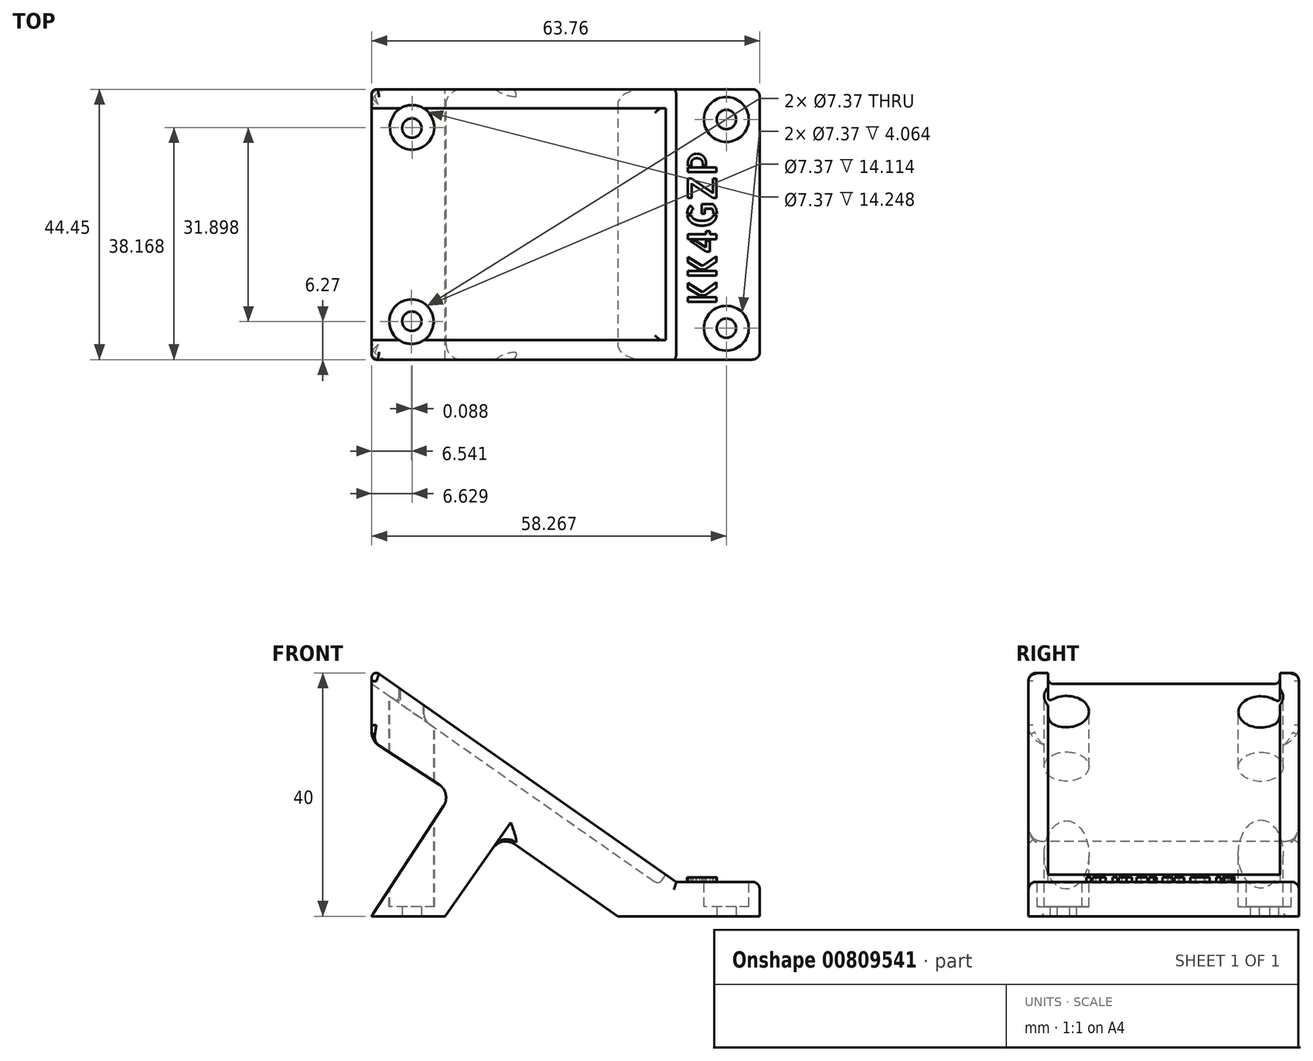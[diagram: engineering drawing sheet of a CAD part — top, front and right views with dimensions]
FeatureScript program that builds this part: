
annotation { "Feature Type Name" : "Feature", "Feature Type Description" : "" }
export const myFeature = defineFeature(function(context is Context, id is Id, definition is map)
    precondition{}
    {
        {
            var Q0;
            Q0=qCreatedBy(makeId("Top.planeOp"),FACE);
            var sketch = newSketch(context, id + "F0", { "sketchPlane" : qUnion([Q0])});
            skPoint(sketch, "E0.middle", {"position": v(0, 0) * mm});
            skCircle(sketch, "E1", {"center": v(-26.75, 16.45) * mm, "radius": 1.59 * mm});
            skCircle(sketch, "E2", {"center": v(-26.75, -15.3) * mm, "radius": 1.59 * mm});
            skCircle(sketch, "E3", {"center": v(24.92, 17.87) * mm, "radius": 1.59 * mm});
            skCircle(sketch, "E4", {"center": v(24.92, -16.44) * mm, "radius": 1.59 * mm});
            skLineSegment(sketch, "E5.0", {"start": v(30.4, 22.84) * mm, "end": v(-33.35, 22.84) * mm});
            skLineSegment(sketch, "E5.1", {"start": v(30.4, 22.84) * mm, "end": v(30.4, -21.6) * mm});
            skLineSegment(sketch, "E5.2", {"start": v(30.4, -21.6) * mm, "end": v(-33.35, -21.6) * mm});
            skLineSegment(sketch, "E5.3", {"start": v(-33.35, 22.84) * mm, "end": v(-33.35, -21.6) * mm});
            skSolve(sketch);
        }
        {
            var Q0;
            Q0=makeQuery(id+"F0.imprint","IMPRINT",FACE,{"disambiguationData":[TD([[makeQuery(id+"F0.imprint","IMPRINT",EDGE,{"derivedFrom":sQuery(id+"F0.wireOp",EDGE,"E1")}),-1.0]])]});
            extrude(context, id + "F1", {"entities" : qUnion([Q0]), "depth" : 50.8 * mm, "offsetDistance" : 25.4 * mm});
        }
        {
            var Q0;
            Q0=qCreatedBy(makeId("Front.planeOp"),FACE);
            var sketch = newSketch(context, id + "F2", { "sketchPlane" : qUnion([Q0])});
            skLineSegment(sketch, "E6", {"start": v(-55.66, 56.32) * mm, "end": v(16.7, 5.65) * mm});
            skLineSegment(sketch, "E7", {"start": v(16.7, 5.65) * mm, "end": v(44.17, 5.65) * mm});
            skLineSegment(sketch, "E8", {"start": v(44.17, 5.65) * mm, "end": v(44.17, 60.47) * mm});
            skLineSegment(sketch, "E9", {"start": v(44.17, 60.47) * mm, "end": v(-55.66, 56.32) * mm});
            skSolve(sketch);
        }
        {
            var Q0;
            Q0=makeQuery(id+"F2.imprint","IMPRINT",FACE,{"disambiguationData":[TD([[makeQuery(id+"F2.imprint","IMPRINT",EDGE,{"derivedFrom":sQuery(id+"F2.wireOp",EDGE,"E6")}),1.0]])]});
            extrude(context, id + "F3", {"entities" : qUnion([Q0]), "operationType" : NewBodyOperationType.REMOVE, "oppositeDirection" : true, "depth" : 76.2 * mm, "offsetDistance" : 25.4 * mm, "symmetric" : true});
        }
        {
            var Q0;
            Q0=makeQuery(id+"F3.boolean.opBoolean","COPY",FACE,{"derivedFrom":makeQuery(id+"F3.opExtrude","SWEPT_FACE",FACE,{"disambiguationData":[OSD([sQuery(id+"F2.wireOp",EDGE,"E6")])]})});
            var sketch = newSketch(context, id + "F4", { "sketchPlane" : qUnion([Q0])});
            skLineSegment(sketch, "E10.bottom", {"start": v(-54.48, 19.71) * mm, "end": v(8.35, 19.71) * mm});
            skLineSegment(sketch, "E10.top", {"start": v(-54.48, -18.39) * mm, "end": v(8.35, -18.39) * mm});
            skLineSegment(sketch, "E10.left", {"start": v(-54.48, 19.71) * mm, "end": v(-54.48, -18.39) * mm});
            skLineSegment(sketch, "E10.right", {"start": v(8.35, 19.71) * mm, "end": v(8.35, -18.39) * mm});
            skSolve(sketch);
        }
        {
            var Q0;
            Q0 = qSketchRegion(id + "F4", true);
            extrude(context, id + "F5", {"entities" : qUnion([Q0]), "operationType" : NewBodyOperationType.REMOVE, "oppositeDirection" : true, "depth" : 2.03 * mm, "offsetDistance" : 25.4 * mm});
        }
        {
            var Q0;
            Q0=makeQuery(id+"F3.boolean.opBoolean","COPY",FACE,{"derivedFrom":makeQuery(id+"F3.opExtrude","SWEPT_FACE",FACE,{"disambiguationData":[OSD([sQuery(id+"F2.wireOp",EDGE,"E7")])]})});
            var sketch = newSketch(context, id + "F6", { "sketchPlane" : qUnion([Q0])});
            skCircle(sketch, "E11", {"center": v(24.92, 17.87) * mm, "radius": 3.68 * mm});
            skCircle(sketch, "E12", {"center": v(24.92, -16.44) * mm, "radius": 3.68 * mm});
            skCircle(sketch, "E13", {"center": v(-26.8, -15.34) * mm, "radius": 3.68 * mm});
            skCircle(sketch, "E14", {"center": v(-26.72, 16.56) * mm, "radius": 3.68 * mm});
            skSolve(sketch);
        }
        {
            var Q0;
            Q0 = qSketchRegion(id + "F6", true);
            extrude(context, id + "F7", {"entities" : qUnion([Q0]), "operationType" : NewBodyOperationType.REMOVE, "oppositeDirection" : true, "depth" : 4.06 * mm, "offsetDistance" : 25.4 * mm, "hasSecondDirection" : true, "secondDirectionOppositeDirection" : false, "secondDirectionDepth" : 50.8 * mm});
        }
        {
            var Q0;
            Q0=makeQuery(id+"F3.boolean.opBoolean","INTERSECT",EDGE,{"derivedFrom":[makeQuery(id+"F1.opExtrude","SWEPT_FACE",FACE,{"disambiguationData":[OSD([sQuery(id+"F0.wireOp",EDGE,"E5.2")])]}),makeQuery(id+"F3.opExtrude","SWEPT_FACE",FACE,{"disambiguationData":[OSD([sQuery(id+"F2.wireOp",EDGE,"E7")])]})]});
            var Q1;
            Q1=makeQuery(id+"FOz7J2DfmrePzTN_1.boolean.opBoolean","INTERSECT",EDGE,{"derivedFrom":[makeQuery(id+"F1.opExtrude","SWEPT_FACE",FACE,{"disambiguationData":[OSD([sQuery(id+"F0.wireOp",EDGE,"E5.2")])]}),makeQuery(id+"FOz7J2DfmrePzTN_1.opExtrude","SWEPT_FACE",FACE,{"disambiguationData":[OSD([sQuery(id+"FwJpcnfpDOWBhRW_1.wireOp",EDGE,"7TAsQrwD-nJ7S-N01j-4NwB-wfjMZ5C82BP1")])]})]});
            var Q2;
            Q2=makeQuery(id+"FOz7J2DfmrePzTN_1.boolean.opBoolean","INTERSECT",EDGE,{"derivedFrom":[makeQuery(id+"F1.opExtrude","SWEPT_FACE",FACE,{"disambiguationData":[OSD([sQuery(id+"F0.wireOp",EDGE,"E5.2")])]}),makeQuery(id+"FOz7J2DfmrePzTN_1.opExtrude","SWEPT_FACE",FACE,{"disambiguationData":[OSD([sQuery(id+"FwJpcnfpDOWBhRW_1.wireOp",EDGE,"6dGtPzXd-V9vu-5sIf-QmpP-IY3SuzzBftYZ")])]})]});
            var Q3;
            Q3=makeQuery(id+"FOz7J2DfmrePzTN_1.boolean.opBoolean","INTERSECT",EDGE,{"derivedFrom":[makeQuery(id+"F1.opExtrude","SWEPT_FACE",FACE,{"disambiguationData":[OSD([sQuery(id+"F0.wireOp",EDGE,"E5.2")])]}),makeQuery(id+"FOz7J2DfmrePzTN_1.opExtrude","SWEPT_FACE",FACE,{"disambiguationData":[OSD([sQuery(id+"FwJpcnfpDOWBhRW_1.wireOp",EDGE,"HFOe4aiu-vJgC-u0Dz-aEjB-NTL0ylJjOqHZ")])]})]});
            var Q4;
            Q4=makeQuery(id+"FOz7J2DfmrePzTN_1.boolean.opBoolean","INTERSECT",EDGE,{"derivedFrom":[makeQuery(id+"F1.opExtrude","SWEPT_FACE",FACE,{"disambiguationData":[OSD([sQuery(id+"F0.wireOp",EDGE,"E5.2")])]}),makeQuery(id+"FOz7J2DfmrePzTN_1.opExtrude","SWEPT_FACE",FACE,{"disambiguationData":[OSD([sQuery(id+"FwJpcnfpDOWBhRW_1.wireOp",EDGE,"6FotfcRq-kzrp-HAaR-29gi-kztGfECXmqdc")])]})]});
            var Q5;
            Q5=makeQuery(id+"Fn8nH9Q8Esl1Hek_1.boolean.opBoolean","INTERSECT",EDGE,{"derivedFrom":[makeQuery(id+"F1.opExtrude","SWEPT_FACE",FACE,{"disambiguationData":[OSD([sQuery(id+"F0.wireOp",EDGE,"E5.2")])]}),makeQuery(id+"Fn8nH9Q8Esl1Hek_1.opExtrude","SWEPT_FACE",FACE,{"disambiguationData":[OSD([sQuery(id+"F2zjoIBAfDjMboZ_1.wireOp",EDGE,"NsKbtacR-0WmU-dClk-nRrQ-DuOnGeB0pbxx")])]})]});
            var Q6;
            Q6=makeQuery(id+"Fn8nH9Q8Esl1Hek_1.boolean.opBoolean","INTERSECT",EDGE,{"derivedFrom":[makeQuery(id+"F1.opExtrude","SWEPT_FACE",FACE,{"disambiguationData":[OSD([sQuery(id+"F0.wireOp",EDGE,"E5.0")])]}),makeQuery(id+"Fn8nH9Q8Esl1Hek_1.opExtrude","SWEPT_FACE",FACE,{"disambiguationData":[OSD([sQuery(id+"F2zjoIBAfDjMboZ_1.wireOp",EDGE,"NsKbtacR-0WmU-dClk-nRrQ-DuOnGeB0pbxx")])]})]});
            var Q7;
            Q7=makeQuery(id+"F3.boolean.opBoolean","INTERSECT",EDGE,{"derivedFrom":[makeQuery(id+"F1.opExtrude","SWEPT_FACE",FACE,{"disambiguationData":[OSD([sQuery(id+"F0.wireOp",EDGE,"E5.0")])]}),makeQuery(id+"F3.opExtrude","SWEPT_FACE",FACE,{"disambiguationData":[OSD([sQuery(id+"F2.wireOp",EDGE,"E6")])]})]});
            var Q8;
            Q8=makeQuery(id+"F3.boolean.opBoolean","INTERSECT",EDGE,{"derivedFrom":[makeQuery(id+"F1.opExtrude","SWEPT_FACE",FACE,{"disambiguationData":[OSD([sQuery(id+"F0.wireOp",EDGE,"E5.0")])]}),makeQuery(id+"F3.opExtrude","SWEPT_FACE",FACE,{"disambiguationData":[OSD([sQuery(id+"F2.wireOp",EDGE,"E7")])]})]});
            var Q9;
            Q9=makeQuery(id+"FOz7J2DfmrePzTN_1.boolean.opBoolean","INTERSECT",EDGE,{"derivedFrom":[makeQuery(id+"F1.opExtrude","SWEPT_FACE",FACE,{"disambiguationData":[OSD([sQuery(id+"F0.wireOp",EDGE,"E5.0")])]}),makeQuery(id+"FOz7J2DfmrePzTN_1.opExtrude","SWEPT_FACE",FACE,{"disambiguationData":[OSD([sQuery(id+"FwJpcnfpDOWBhRW_1.wireOp",EDGE,"HFOe4aiu-vJgC-u0Dz-aEjB-NTL0ylJjOqHZ")])]})]});
            var Q10;
            Q10=makeQuery(id+"FOz7J2DfmrePzTN_1.boolean.opBoolean","INTERSECT",EDGE,{"derivedFrom":[makeQuery(id+"F1.opExtrude","SWEPT_FACE",FACE,{"disambiguationData":[OSD([sQuery(id+"F0.wireOp",EDGE,"E5.0")])]}),makeQuery(id+"FOz7J2DfmrePzTN_1.opExtrude","SWEPT_FACE",FACE,{"disambiguationData":[OSD([sQuery(id+"FwJpcnfpDOWBhRW_1.wireOp",EDGE,"6dGtPzXd-V9vu-5sIf-QmpP-IY3SuzzBftYZ")])]})]});
            var Q11;
            Q11=makeQuery(id+"FOz7J2DfmrePzTN_1.boolean.opBoolean","INTERSECT",EDGE,{"derivedFrom":[makeQuery(id+"F1.opExtrude","SWEPT_FACE",FACE,{"disambiguationData":[OSD([sQuery(id+"F0.wireOp",EDGE,"E5.0")])]}),makeQuery(id+"FOz7J2DfmrePzTN_1.opExtrude","SWEPT_FACE",FACE,{"disambiguationData":[OSD([sQuery(id+"FwJpcnfpDOWBhRW_1.wireOp",EDGE,"7TAsQrwD-nJ7S-N01j-4NwB-wfjMZ5C82BP1")])]})]});
            var Q12;
            Q12=makeQuery(id+"FOz7J2DfmrePzTN_1.boolean.opBoolean","INTERSECT",EDGE,{"derivedFrom":[makeQuery(id+"F1.opExtrude","SWEPT_FACE",FACE,{"disambiguationData":[OSD([sQuery(id+"F0.wireOp",EDGE,"E5.0")])]}),makeQuery(id+"FOz7J2DfmrePzTN_1.opExtrude","SWEPT_FACE",FACE,{"disambiguationData":[OSD([sQuery(id+"FwJpcnfpDOWBhRW_1.wireOp",EDGE,"6FotfcRq-kzrp-HAaR-29gi-kztGfECXmqdc")])]})]});
            var Q13;
            Q13=makeQuery(id+"F1.opExtrude","CAP_EDGE",EDGE,{"disambiguationData":[OSD([sQuery(id+"F0.wireOp",EDGE,"E5.0")])],"isStart":false});
            var Q14;
            Q14=makeQuery(id+"F1.opExtrude","CAP_EDGE",EDGE,{"disambiguationData":[OSD([sQuery(id+"F0.wireOp",EDGE,"E5.2")])],"isStart":false});
            var Q15;
            Q15=makeQuery(id+"F3.boolean.opBoolean","INTERSECT",EDGE,{"derivedFrom":[makeQuery(id+"F1.opExtrude","SWEPT_FACE",FACE,{"disambiguationData":[OSD([sQuery(id+"F0.wireOp",EDGE,"E5.2")])]}),makeQuery(id+"F3.opExtrude","SWEPT_FACE",FACE,{"disambiguationData":[OSD([sQuery(id+"F2.wireOp",EDGE,"E6")])]})]});
            fillet(context, id + "F8", {"entities" : qUnion([Q0, Q1, Q2, Q3, Q4, Q5, Q6, Q7, Q8, Q9, Q10, Q11, Q12, Q13, Q14, Q15]), "radius" : 1.27 * mm, "tangentPropagation" : true, "allowEdgeOverflow" : false});
        }
        {
            var Q0;
            Q0=qCreatedBy(makeId("Front.planeOp"),FACE);
            var sketch = newSketch(context, id + "F9", { "sketchPlane" : qUnion([Q0])});
            skLineSegment(sketch, "E15.0", {"start": v(11.2, -2.9) * mm, "end": v(-11.94, 13.31) * mm});
            skLineSegment(sketch, "E16", {"start": v(-20.87, -3.55) * mm, "end": v(11.2, -2.9) * mm});
            skLineSegment(sketch, "E17", {"start": v(-11.94, 13.31) * mm, "end": v(-23.91, -3.78) * mm});
            skLineSegment(sketch, "E18", {"start": v(-20.87, -3.55) * mm, "end": v(-23.91, -3.78) * mm});
            skSolve(sketch);
        }
        {
            var Q0;
            Q0 = qSketchRegion(id + "F9", true);
            extrude(context, id + "F10", {"entities" : qUnion([Q0]), "operationType" : NewBodyOperationType.REMOVE, "depth" : 76.2 * mm, "offsetDistance" : 25.4 * mm, "symmetric" : true});
        }
        {
            var Q0;
            Q0=makeQuery(id+"F10.boolean.opBoolean","INTERSECT",EDGE,{"derivedFrom":[makeQuery(id+"F1.opExtrude","SWEPT_FACE",FACE,{"disambiguationData":[OSD([sQuery(id+"F0.wireOp",EDGE,"E5.2")])]}),makeQuery(id+"F10.opExtrude","SWEPT_FACE",FACE,{"disambiguationData":[OSD([sQuery(id+"F9.wireOp",EDGE,"E15.0")])]})]});
            var Q1;
            Q1=makeQuery(id+"F10.boolean.opBoolean","INTERSECT",EDGE,{"derivedFrom":[makeQuery(id+"F1.opExtrude","SWEPT_FACE",FACE,{"disambiguationData":[OSD([sQuery(id+"F0.wireOp",EDGE,"E5.2")])]}),makeQuery(id+"F10.opExtrude","SWEPT_FACE",FACE,{"disambiguationData":[OSD([sQuery(id+"F9.wireOp",EDGE,"ccf1a9ce-37c2-4cbf-8fa8-a78777553da6.0")])]})]});
            var Q2;
            Q2=makeQuery(id+"F10.boolean.opBoolean","INTERSECT",EDGE,{"derivedFrom":[makeQuery(id+"F1.opExtrude","SWEPT_FACE",FACE,{"disambiguationData":[OSD([sQuery(id+"F0.wireOp",EDGE,"E5.0")])]}),makeQuery(id+"F10.opExtrude","SWEPT_FACE",FACE,{"disambiguationData":[OSD([sQuery(id+"F9.wireOp",EDGE,"ccf1a9ce-37c2-4cbf-8fa8-a78777553da6.0")])]})]});
            var Q3;
            Q3=makeQuery(id+"F10.boolean.opBoolean","INTERSECT",EDGE,{"derivedFrom":[makeQuery(id+"F1.opExtrude","SWEPT_FACE",FACE,{"disambiguationData":[OSD([sQuery(id+"F0.wireOp",EDGE,"E5.0")])]}),makeQuery(id+"F10.opExtrude","SWEPT_FACE",FACE,{"disambiguationData":[OSD([sQuery(id+"F9.wireOp",EDGE,"E15.0")])]})]});
            fillet(context, id + "F11", {"entities" : qUnion([Q0, Q1, Q2, Q3]), "radius" : 2.54 * mm, "tangentPropagation" : true, "allowEdgeOverflow" : false});
        }
        {
            var Q0;
            Q0=makeQuery(id+"F5.boolean.opBoolean","COPY",EDGE,{"derivedFrom":makeQuery(id+"F5.opExtrude","CAP_EDGE",EDGE,{"disambiguationData":[OSD([sQuery(id+"F4.wireOp",EDGE,"E10.right")])],"isStart":true})});
            var Q1;
            Q1=makeQuery(id+"F5.boolean.opBoolean","COPY",EDGE,{"derivedFrom":makeQuery(id+"F5.opExtrude","CAP_EDGE",EDGE,{"disambiguationData":[OSD([sQuery(id+"F4.wireOp",EDGE,"E10.bottom")])],"isStart":true})});
            var Q2;
            Q2=makeQuery(id+"F5.boolean.opBoolean","COPY",EDGE,{"derivedFrom":makeQuery(id+"F5.opExtrude","CAP_EDGE",EDGE,{"disambiguationData":[OSD([sQuery(id+"F4.wireOp",EDGE,"E10.top")])],"isStart":true})});
            var Q3;
            Q3=makeQuery(id+"F5.boolean.opBoolean","COPY",EDGE,{"derivedFrom":makeQuery(id+"F5.opExtrude","CAP_EDGE",EDGE,{"disambiguationData":[OSD([sQuery(id+"F4.wireOp",EDGE,"E10.right")])],"isStart":false})});
            var Q4;
            Q4=makeQuery(id+"F5.boolean.opBoolean","COPY",EDGE,{"derivedFrom":makeQuery(id+"F5.opExtrude","CAP_EDGE",EDGE,{"disambiguationData":[OSD([sQuery(id+"F4.wireOp",EDGE,"E10.bottom")])],"isStart":false})});
            var Q5;
            Q5=makeQuery(id+"F5.boolean.opBoolean","COPY",EDGE,{"derivedFrom":makeQuery(id+"F5.opExtrude","CAP_EDGE",EDGE,{"disambiguationData":[OSD([sQuery(id+"F4.wireOp",EDGE,"E10.top")])],"isStart":false})});
            var Q6;
            Q6=makeQuery(id+"F5.boolean.opBoolean","INTERSECT",EDGE,{"derivedFrom":[makeQuery(id+"F1.opExtrude","CAP_FACE",FACE,{"disambiguationData":[OSD([sQuery(id+"F0.wireOp",EDGE,"E1"),sQuery(id+"F0.wireOp",EDGE,"E2"),sQuery(id+"F0.wireOp",EDGE,"E3"),sQuery(id+"F0.wireOp",EDGE,"E4"),sQuery(id+"F0.wireOp",EDGE,"E5.0"),sQuery(id+"F0.wireOp",EDGE,"E5.1"),sQuery(id+"F0.wireOp",EDGE,"E5.2"),sQuery(id+"F0.wireOp",EDGE,"E5.3")])],"isStart":false}),makeQuery(id+"F5.opExtrude","SWEPT_FACE",FACE,{"disambiguationData":[OSD([sQuery(id+"F4.wireOp",EDGE,"E10.top")])]})]});
            var Q7;
            Q7=makeQuery(id+"F5.boolean.opBoolean","INTERSECT",EDGE,{"derivedFrom":[makeQuery(id+"F1.opExtrude","CAP_FACE",FACE,{"disambiguationData":[OSD([sQuery(id+"F0.wireOp",EDGE,"E1"),sQuery(id+"F0.wireOp",EDGE,"E2"),sQuery(id+"F0.wireOp",EDGE,"E3"),sQuery(id+"F0.wireOp",EDGE,"E4"),sQuery(id+"F0.wireOp",EDGE,"E5.0"),sQuery(id+"F0.wireOp",EDGE,"E5.1"),sQuery(id+"F0.wireOp",EDGE,"E5.2"),sQuery(id+"F0.wireOp",EDGE,"E5.3")])],"isStart":false}),makeQuery(id+"F5.opExtrude","SWEPT_FACE",FACE,{"disambiguationData":[OSD([sQuery(id+"F4.wireOp",EDGE,"E10.bottom")])]})]});
            fillet(context, id + "F12", {"entities" : qUnion([Q0, Q1, Q2, Q3, Q4, Q5, Q6, Q7]), "radius" : 0.76 * mm, "tangentPropagation" : true, "allowEdgeOverflow" : false});
        }
        {
            var Q0;
            Q0=makeQuery(id+"F3.boolean.opBoolean","COPY",FACE,{"derivedFrom":makeQuery(id+"F3.opExtrude","SWEPT_FACE",FACE,{"disambiguationData":[OSD([sQuery(id+"F2.wireOp",EDGE,"E7")])]})});
            var sketch = newSketch(context, id + "F13", { "sketchPlane" : qUnion([Q0])});
            skText(sketch, "E19", { "text": "KK4GZP", "fontName": "AllertaStencil-Regular.ttf"});
            skPoint(sketch, "E20", {"position": v(27.25, 0) * mm});
            const initialGuessF13  = {"E19": [0.02331, -0.0127, 0, 1, 0.00475]};
            skSetInitialGuess(sketch, initialGuessF13);
            skSolve(sketch);
        }
        {
            var Q0;
            Q0 = qSketchRegion(id + "F13", true);
            extrude(context, id + "F14", {"entities" : qUnion([Q0]), "operationType" : NewBodyOperationType.ADD, "depth" : 0.76 * mm, "offsetDistance" : 25.4 * mm});
        }
        {
            var Q0;
            Q0=qCreatedBy(makeId("Front.planeOp"),FACE);
            var sketch = newSketch(context, id + "F15", { "sketchPlane" : qUnion([Q0])});
            skLineSegment(sketch, "E21", {"start": v(-41.67, 34.33) * mm, "end": v(-20.15, 20.25) * mm});
            skLineSegment(sketch, "E22", {"start": v(-20.15, 20.25) * mm, "end": v(-34.3, -1.36) * mm});
            skLineSegment(sketch, "E23", {"start": v(-34.3, -1.36) * mm, "end": v(-54.77, 18.88) * mm});
            skLineSegment(sketch, "E24", {"start": v(-54.77, 18.88) * mm, "end": v(-41.67, 34.33) * mm});
            skSolve(sketch);
        }
        {
            var Q0;
            Q0=makeQuery(id+"F15.imprint","IMPRINT",FACE,{"disambiguationData":[TD([[makeQuery(id+"F15.imprint","IMPRINT",EDGE,{"derivedFrom":sQuery(id+"F15.wireOp",EDGE,"E21")}),-1.0]])]});
            extrude(context, id + "F16", {"entities" : qUnion([Q0]), "operationType" : NewBodyOperationType.REMOVE, "oppositeDirection" : true, "depth" : 76.2 * mm, "offsetDistance" : 25.4 * mm, "symmetric" : true});
        }
        {
            var Q0;
            Q0=makeQuery(id+"F16.boolean.opBoolean","INTERSECT",EDGE,{"derivedFrom":[makeQuery(id+"F1.opExtrude","SWEPT_FACE",FACE,{"disambiguationData":[OSD([sQuery(id+"F0.wireOp",EDGE,"E5.2")])]}),makeQuery(id+"F16.opExtrude","SWEPT_FACE",FACE,{"disambiguationData":[OSD([sQuery(id+"F15.wireOp",EDGE,"E21")])]})]});
            var Q1;
            Q1=makeQuery(id+"F16.boolean.opBoolean","COPY",EDGE,{"derivedFrom":makeQuery(id+"F16.opExtrude","SWEPT_EDGE",EDGE,{"disambiguationData":[OSD([sQuery(id+"F15.wireOp",EDGE,"E21"),sQuery(id+"F15.wireOp",EDGE,"E22")])]})});
            var Q2;
            Q2=makeQuery(id+"F16.boolean.opBoolean","INTERSECT",EDGE,{"derivedFrom":[makeQuery(id+"F1.opExtrude","SWEPT_FACE",FACE,{"disambiguationData":[OSD([sQuery(id+"F0.wireOp",EDGE,"E5.2")])]}),makeQuery(id+"F16.opExtrude","SWEPT_FACE",FACE,{"disambiguationData":[OSD([sQuery(id+"F15.wireOp",EDGE,"E22")])]})]});
            var Q3;
            Q3=makeQuery(id+"F16.boolean.opBoolean","INTERSECT",EDGE,{"derivedFrom":[makeQuery(id+"F1.opExtrude","SWEPT_FACE",FACE,{"disambiguationData":[OSD([sQuery(id+"F0.wireOp",EDGE,"E5.0")])]}),makeQuery(id+"F16.opExtrude","SWEPT_FACE",FACE,{"disambiguationData":[OSD([sQuery(id+"F15.wireOp",EDGE,"E22")])]})]});
            var Q4;
            Q4=makeQuery(id+"F16.boolean.opBoolean","INTERSECT",EDGE,{"derivedFrom":[makeQuery(id+"F1.opExtrude","SWEPT_FACE",FACE,{"disambiguationData":[OSD([sQuery(id+"F0.wireOp",EDGE,"E5.0")])]}),makeQuery(id+"F16.opExtrude","SWEPT_FACE",FACE,{"disambiguationData":[OSD([sQuery(id+"F15.wireOp",EDGE,"E21")])]})]});
            var Q5;
            Q5=makeQuery(id+"F16.boolean.opBoolean","INTERSECT",EDGE,{"derivedFrom":[makeQuery(id+"F1.opExtrude","SWEPT_FACE",FACE,{"disambiguationData":[OSD([sQuery(id+"F0.wireOp",EDGE,"E5.3")])]}),makeQuery(id+"F16.opExtrude","SWEPT_FACE",FACE,{"disambiguationData":[OSD([sQuery(id+"F15.wireOp",EDGE,"E22")])]})]});
            var Q6;
            Q6=makeQuery(id+"F16.boolean.opBoolean","INTERSECT",EDGE,{"derivedFrom":[makeQuery(id+"F1.opExtrude","SWEPT_FACE",FACE,{"disambiguationData":[OSD([sQuery(id+"F0.wireOp",EDGE,"E5.3")])]}),makeQuery(id+"F16.opExtrude","SWEPT_FACE",FACE,{"disambiguationData":[OSD([sQuery(id+"F15.wireOp",EDGE,"E21")])]})]});
            var Q7;
            Q7=makeQuery(id+"F10.boolean.opBoolean","COPY",EDGE,{"derivedFrom":makeQuery(id+"F10.opExtrude","SWEPT_EDGE",EDGE,{"disambiguationData":[OSD([sQuery(id+"F9.wireOp",EDGE,"E15.0"),sQuery(id+"F9.wireOp",EDGE,"E17")])]})});
            fillet(context, id + "F17", {"entities" : qUnion([Q0, Q1, Q2, Q3, Q4, Q5, Q6, Q7]), "radius" : 2.54 * mm, "tangentPropagation" : true, "allowEdgeOverflow" : false});
        }
        {
            var Q0;
            Q0=makeQuery(id+"F3.boolean.opBoolean","INTERSECT",EDGE,{"derivedFrom":[makeQuery(id+"F1.opExtrude","SWEPT_FACE",FACE,{"disambiguationData":[OSD([sQuery(id+"F0.wireOp",EDGE,"E5.1")])]}),makeQuery(id+"F3.opExtrude","SWEPT_FACE",FACE,{"disambiguationData":[OSD([sQuery(id+"F2.wireOp",EDGE,"E7")])]})]});
            var Q1;
            Q1=makeQuery(id+"F8.opFillet","BLEND_EDGE",EDGE,{"blendedFrom":[makeQuery(id+"F3.boolean.opBoolean","INTERSECT",EDGE,{"derivedFrom":[makeQuery(id+"F1.opExtrude","SWEPT_FACE",FACE,{"disambiguationData":[OSD([sQuery(id+"F0.wireOp",EDGE,"E5.2")])]}),makeQuery(id+"F3.opExtrude","SWEPT_FACE",FACE,{"disambiguationData":[OSD([sQuery(id+"F2.wireOp",EDGE,"E7")])]})]}),makeQuery(id+"F1.opExtrude","SWEPT_FACE",FACE,{"disambiguationData":[OSD([sQuery(id+"F0.wireOp",EDGE,"E5.1")])]})],"blendedInto":[makeQuery(id+"F1.opExtrude","SWEPT_FACE",FACE,{"disambiguationData":[OSD([sQuery(id+"F0.wireOp",EDGE,"E5.1")])]})]});
            var Q2;
            Q2=makeQuery(id+"F1.opExtrude","SWEPT_EDGE",EDGE,{"disambiguationData":[OSD([sQuery(id+"F0.wireOp",EDGE,"E5.0"),sQuery(id+"F0.wireOp",EDGE,"E5.1")])]});
            var Q3;
            Q3=makeQuery(id+"F8.opFillet","BLEND_EDGE",EDGE,{"blendedFrom":[makeQuery(id+"F3.boolean.opBoolean","INTERSECT",EDGE,{"derivedFrom":[makeQuery(id+"F1.opExtrude","SWEPT_FACE",FACE,{"disambiguationData":[OSD([sQuery(id+"F0.wireOp",EDGE,"E5.0")])]}),makeQuery(id+"F3.opExtrude","SWEPT_FACE",FACE,{"disambiguationData":[OSD([sQuery(id+"F2.wireOp",EDGE,"E7")])]})]}),makeQuery(id+"F1.opExtrude","SWEPT_FACE",FACE,{"disambiguationData":[OSD([sQuery(id+"F0.wireOp",EDGE,"E5.1")])]})],"blendedInto":[makeQuery(id+"F1.opExtrude","SWEPT_FACE",FACE,{"disambiguationData":[OSD([sQuery(id+"F0.wireOp",EDGE,"E5.1")])]})]});
            var Q4;
            Q4=makeQuery(id+"F1.opExtrude","SWEPT_EDGE",EDGE,{"disambiguationData":[OSD([sQuery(id+"F0.wireOp",EDGE,"E5.1"),sQuery(id+"F0.wireOp",EDGE,"E5.2")])]});
            fillet(context, id + "F18", {"entities" : qUnion([Q0, Q1, Q2, Q3, Q4]), "radius" : 1.27 * mm, "tangentPropagation" : true, "allowEdgeOverflow" : false});
        }
        {
            var Q0;
            {var subQ0=sQuery(id+"F0.wireOp",EDGE,"E5.0");var subQ1=sQuery(id+"F0.wireOp",EDGE,"E5.3");Q0=makeQuery(id+"F16.boolean.opBoolean","SPLIT",EDGE,{"disambiguationData":[TD([makeQuery(id+"F16.opExtrude","SWEPT_FACE",FACE,{"disambiguationData":[OSD([sQuery(id+"F15.wireOp",EDGE,"E21")])]})])],"derivedFrom":makeQuery(id+"F1.opExtrude","SWEPT_EDGE",EDGE,{"disambiguationData":[OSD([subQ0,subQ1])]})});}
            var Q1;
            {var subQ0=sQuery(id+"F0.wireOp",EDGE,"E5.2");var subQ1=sQuery(id+"F0.wireOp",EDGE,"E5.3");Q1=makeQuery(id+"F16.boolean.opBoolean","SPLIT",EDGE,{"disambiguationData":[TD([makeQuery(id+"F16.opExtrude","SWEPT_FACE",FACE,{"disambiguationData":[OSD([sQuery(id+"F15.wireOp",EDGE,"E21")])]})])],"derivedFrom":makeQuery(id+"F1.opExtrude","SWEPT_EDGE",EDGE,{"disambiguationData":[OSD([subQ0,subQ1])]})});}
            fillet(context, id + "F19", {"entities" : qUnion([Q0, Q1]), "radius" : 0.76 * mm, "tangentPropagation" : true, "allowEdgeOverflow" : false});
        }
    });
